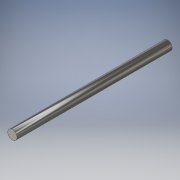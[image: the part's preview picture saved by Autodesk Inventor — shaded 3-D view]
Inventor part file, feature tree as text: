
AUTODESK INVENTOR PART (.ipt)
format: ipt  version: 2019 (Build 230136000, 136)  size: 100,352 bytes
history: native  units: mm
features: other x1, extrude x1, sketch x1
ambient origin geometry x8: Origin, YZ Plane, XZ Plane, XY Plane, X Axis, Y Axis, Z Axis, Center Point
bodies: Body1 (feature_tree)
feature tree (3):
  other  "Твердое тело1"
  extrude  "Выдавливание1"  Depth=6.0mm
  sketch  "Эскиз1"
